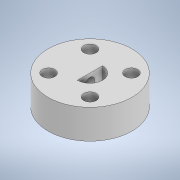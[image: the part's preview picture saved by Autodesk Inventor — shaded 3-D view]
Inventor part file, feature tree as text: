
AUTODESK INVENTOR PART (.ipt)
format: ipt  version: 2022 (Build 260153000, 153)  size: 140,288 bytes
history: native  units: mm
features: extrude x5, sketch x5, plane x1
ambient origin geometry x8: Origin, YZ Plane, XZ Plane, XY Plane, X Axis, Y Axis, Z Axis, Center Point
bodies: Solid1 (feature_tree)
feature tree (11):
  extrude  "Extrusion1"  Depth=7.0mm TaperAngle=0.0deg
  extrude  "Extrusion2"  Depth=6.0mm TaperAngle=0.0deg
  extrude  "Extrusion3"  Depth=1.0mm
  plane  "Work Plane1"
  extrude  "Extrusion4"  Depth=3.0mm
  extrude  "Extrusion5"  Depth=3.0mm
  sketch  "Sketch1"  dims[d0=20.0mm d1=7.0mm d2=0.0mm]
  sketch  "Sketch2"  dims[d3=6.0mm d4=4.0mm d5=0.0mm]
  sketch  "Sketch3"  dims[d6=1.0mm d7=0.0mm d9=2.25mm]
  sketch  "Sketch4"  dims[d10=1.0mm d11=0.0mm d14=3.0mm]
  sketch  "Sketch5"  dims[d15=40.0mm d17=360.0deg d19=3.0mm d20=0.0mm]
